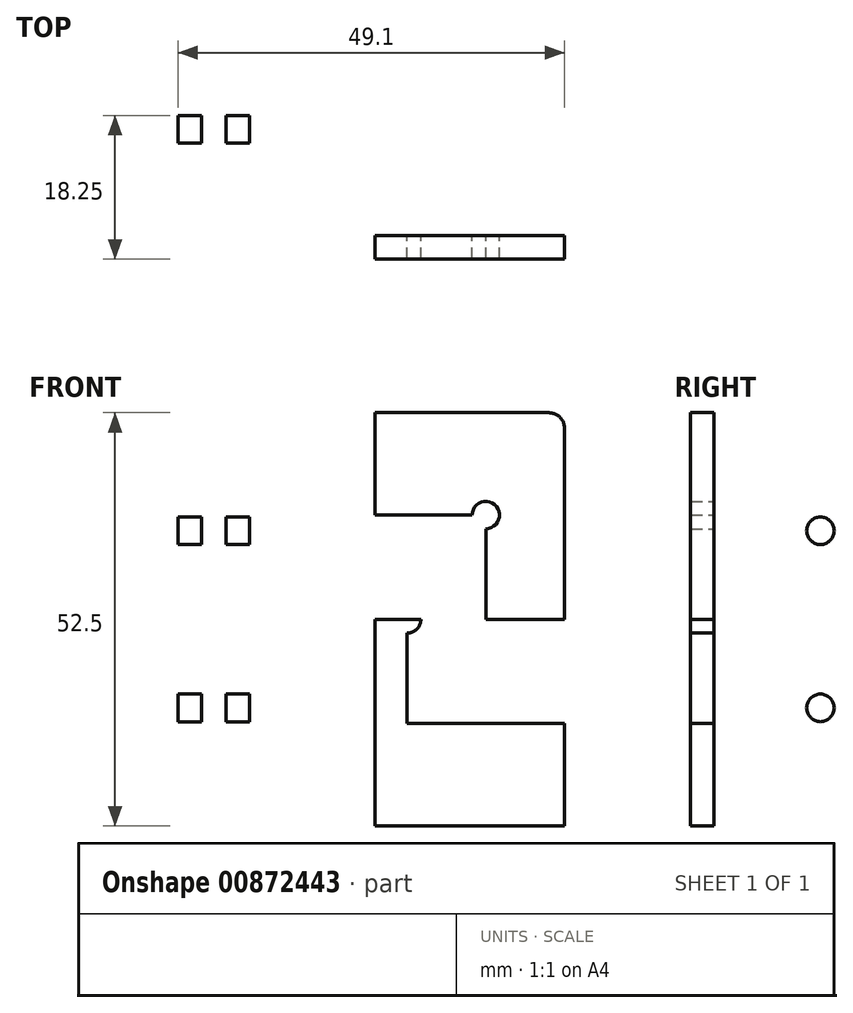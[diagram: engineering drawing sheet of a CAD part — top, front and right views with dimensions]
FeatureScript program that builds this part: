
annotation { "Feature Type Name" : "Feature", "Feature Type Description" : "" }
export const myFeature = defineFeature(function(context is Context, id is Id, definition is map)
    precondition{}
    {
        {
            var Q0;
            Q0=qCreatedBy(makeId("Top.planeOp"),FACE);
            var sketch = newSketch(context, id + "F0", { "sketchPlane" : qUnion([Q0])});
            skLineSegment(sketch, "E0", {"start": v(0, 0) * mm, "end": v(0, 30) * mm});
            skLineSegment(sketch, "E1", {"start": v(0, 30) * mm, "end": v(-3, 30) * mm});
            skLineSegment(sketch, "E2", {"start": v(-3, 30) * mm, "end": v(-3, 0) * mm});
            skLineSegment(sketch, "E3", {"start": v(-3, 0) * mm, "end": v(-6.1, 0) * mm});
            skLineSegment(sketch, "E4", {"start": v(-6.1, 0) * mm, "end": v(-6.1, 30) * mm});
            skLineSegment(sketch, "E5", {"start": v(-6.1, 30) * mm, "end": v(-9.1, 30) * mm});
            skLineSegment(sketch, "E6", {"start": v(-9.1, 30) * mm, "end": v(-9.1, -3) * mm});
            skLineSegment(sketch, "E7", {"start": v(0, 0) * mm, "end": v(40, 0) * mm});
            skLineSegment(sketch, "E8", {"start": v(40, 0) * mm, "end": v(40, -3) * mm});
            skLineSegment(sketch, "E9", {"start": v(-9.1, -3) * mm, "end": v(40, -3) * mm});
            skLineSegment(sketch, "E10", {"start": v(0, 0) * mm, "end": v(-9.1, 0) * mm});
            skSolve(sketch);
        }
        {
            var Q0;
            {var subQ0=sQuery(id+"F0.wireOp",EDGE,"E0");Q0=makeQuery(id+"F0.imprint","IMPRINT",FACE,{"disambiguationData":[TD([[makeQuery(id+"F0.imprint","IMPRINT",EDGE,{"derivedFrom":subQ0}),1.0]])]});}
            var Q1;
            {var subQ0=sQuery(id+"F0.wireOp",EDGE,"E4");Q1=makeQuery(id+"F0.imprint","IMPRINT",FACE,{"disambiguationData":[TD([[makeQuery(id+"F0.imprint","IMPRINT",EDGE,{"derivedFrom":subQ0}),1.0]])]});}
            var Q2;
            {var subQ5=sQuery(id+"F0.wireOp",EDGE,"E3");Q2=makeQuery(id+"F0.imprint","IMPRINT",FACE,{"disambiguationData":[TD([[makeQuery(id+"F0.imprint","IMPRINT",EDGE,{"derivedFrom":subQ5}),1.0]])]});}
            var Q3;
            Q3=sQuery(id+"F0.wireOp",EDGE,"E4");
            var Q4;
            Q4=sQuery(id+"F0.wireOp",EDGE,"E9");
            var Q5;
            Q5=sQuery(id+"F0.wireOp",EDGE,"E7");
            var Q6;
            Q6=sQuery(id+"F0.wireOp",EDGE,"E0");
            var Q7;
            Q7=sQuery(id+"F0.wireOp",EDGE,"E2");
            var Q8;
            Q8=sQuery(id+"F0.wireOp",EDGE,"E6");
            var Q9;
            Q9=sQuery(id+"F0.wireOp",EDGE,"E3");
            var Q10;
            Q10=sQuery(id+"F0.wireOp",EDGE,"E5");
            var Q11;
            Q11=sQuery(id+"F0.wireOp",EDGE,"E8");
            var Q12;
            Q12=sQuery(id+"F0.wireOp",EDGE,"E1");
            extrude(context, id + "F1", {"entities" : qUnion([Q0, Q1, Q2]), "surfaceEntities" : qUnion([Q3, Q4, Q5, Q6, Q7, Q8, Q9, Q10, Q11, Q12]), "depth" : 52.5 * mm, "offsetDistance" : 25 * mm});
        }
        {
            var Q0;
            Q0=makeQuery(id+"F1.opExtrude","SWEPT_FACE",FACE,{"disambiguationData":[OSD([sQuery(id+"F0.wireOp",EDGE,"E6")])]});
            var sketch = newSketch(context, id + "F2", { "sketchPlane" : qUnion([Q0])});
            skLineSegment(sketch, "E11", {"start": v(3, 52.5) * mm, "end": v(3, 0) * mm});
            skLineSegment(sketch, "E12", {"start": v(-13.5, 52.5) * mm, "end": v(-13.5, 0) * mm});
            skLineSegment(sketch, "E13", {"start": v(-13.5, 52.5) * mm, "end": v(-13.5, 37.5) * mm});
            skLineSegment(sketch, "E14", {"start": v(-13.5, 26.25) * mm, "end": v(-13.5, 11.34) * mm});
            skLineSegment(sketch, "E15", {"start": v(-13.5, 0) * mm, "end": v(-13.5, 15) * mm});
            skCircle(sketch, "E16", {"center": v(-13.5, 37.5) * mm, "radius": 1.75 * mm});
            skCircle(sketch, "E17", {"center": v(-13.5, 15) * mm, "radius": 1.75 * mm});
            skSolve(sketch);
        }
        {
            var Q0;
            {var subQ0=sQuery(id+"F2.wireOp",EDGE,"E13");var subQ1=sQuery(id+"F2.wireOp",EDGE,"E12");var subQ2=makeQuery(id+"F2.imprint","INTERSECT",VERTEX,{"derivedFrom":[subQ1,subQ0]});Q0=makeQuery(id+"F2.imprint","IMPRINT",FACE,{"disambiguationData":[TD([[makeQuery(id+"F2.imprint","IMPRINT",EDGE,{"disambiguationData":[TD([[subQ2,-1.0]])],"derivedFrom":subQ1}),-1.0]])]});}
            var Q1;
            {var subQ0=sQuery(id+"F2.wireOp",EDGE,"E13");var subQ1=sQuery(id+"F2.wireOp",EDGE,"E12");var subQ2=makeQuery(id+"F2.imprint","INTERSECT",VERTEX,{"derivedFrom":[subQ1,subQ0]});Q1=makeQuery(id+"F2.imprint","IMPRINT",FACE,{"disambiguationData":[TD([[makeQuery(id+"F2.imprint","IMPRINT",EDGE,{"disambiguationData":[TD([[subQ2,-1.0]])],"derivedFrom":subQ1}),1.0]])]});}
            var Q2;
            {var subQ0=sQuery(id+"F2.wireOp",EDGE,"E15");var subQ1=sQuery(id+"F2.wireOp",EDGE,"E14");var subQ2=makeQuery(id+"F2.imprint","INTERSECT",VERTEX,{"derivedFrom":[subQ1,subQ0]});Q2=makeQuery(id+"F2.imprint","IMPRINT",FACE,{"disambiguationData":[TD([[makeQuery(id+"F2.imprint","IMPRINT",EDGE,{"disambiguationData":[TD([[subQ2,1.0]])],"derivedFrom":subQ1}),1.0]])]});}
            var Q3;
            {var subQ0=sQuery(id+"F2.wireOp",EDGE,"E15");var subQ1=sQuery(id+"F2.wireOp",EDGE,"E14");var subQ2=makeQuery(id+"F2.imprint","INTERSECT",VERTEX,{"derivedFrom":[subQ1,subQ0]});Q3=makeQuery(id+"F2.imprint","IMPRINT",FACE,{"disambiguationData":[TD([[makeQuery(id+"F2.imprint","IMPRINT",EDGE,{"disambiguationData":[TD([[subQ2,1.0]])],"derivedFrom":subQ1}),-1.0]])]});}
            var Q4;
            Q4=sQuery(id+"F2.wireOp",EDGE,"E16");
            var Q5;
            Q5=sQuery(id+"F2.wireOp",EDGE,"E17");
            extrude(context, id + "F3", {"entities" : qUnion([Q0, Q1, Q2, Q3]), "operationType" : NewBodyOperationType.REMOVE, "surfaceEntities" : qUnion([Q4, Q5]), "oppositeDirection" : true, "depth" : 25 * mm, "offsetDistance" : 25 * mm});
        }
        {
            var Q0;
            Q0=makeQuery(id+"F1.opExtrude","SWEPT_FACE",FACE,{"disambiguationData":[OSD([sQuery(id+"F0.wireOp",EDGE,"E7")])]});
            var sketch = newSketch(context, id + "F4", { "sketchPlane" : qUnion([Q0])});
            skLineSegment(sketch, "E18", {"start": v(0, 52.5) * mm, "end": v(-40, 52.5) * mm});
            skLineSegment(sketch, "E19", {"start": v(-40, 0) * mm, "end": v(-30, 0) * mm});
            skLineSegment(sketch, "E20", {"start": v(-30, 0) * mm, "end": v(-20, 0) * mm});
            skLineSegment(sketch, "E21", {"start": v(-20, 0) * mm, "end": v(-10, 0) * mm});
            skLineSegment(sketch, "E22", {"start": v(-20, 0) * mm, "end": v(-20, 52.5) * mm});
            skLineSegment(sketch, "E23", {"start": v(-10, 0) * mm, "end": v(-10, 52.5) * mm});
            skLineSegment(sketch, "E24", {"start": v(-30, 0) * mm, "end": v(-30, 52.5) * mm});
            skLineSegment(sketch, "E25", {"start": v(-40, 52.5) * mm, "end": v(-40, 39.5) * mm});
            skLineSegment(sketch, "E26", {"start": v(-40, 0) * mm, "end": v(-40, 13) * mm});
            skLineSegment(sketch, "E27", {"start": v(-40, 13) * mm, "end": v(-40, 26.25) * mm});
            skLineSegment(sketch, "E28", {"start": v(-40, 26.25) * mm, "end": v(0, 26.25) * mm});
            skLineSegment(sketch, "E29", {"start": v(-40, 13) * mm, "end": v(0, 13) * mm});
            skLineSegment(sketch, "E30", {"start": v(-40, 39.5) * mm, "end": v(0, 39.5) * mm});
            skCircle(sketch, "E31", {"center": v(-30, 39.5) * mm, "radius": 1.75 * mm});
            skCircle(sketch, "E32", {"center": v(-10, 39.5) * mm, "radius": 1.75 * mm});
            skCircle(sketch, "E33", {"center": v(-30, 13) * mm, "radius": 1.75 * mm});
            skCircle(sketch, "E34", {"center": v(-10, 13) * mm, "radius": 1.75 * mm});
            skCircle(sketch, "E35", {"center": v(-20, 26.25) * mm, "radius": 1.75 * mm});
            skSolve(sketch);
        }
        {
            var Q0;
            {var subQ0=sQuery(id+"F4.wireOp",EDGE,"E31");var subQ1=sQuery(id+"F4.wireOp",EDGE,"E24");var subQ2=makeQuery(id+"F4.imprint","INTERSECT",VERTEX,{"disambiguationData":[OD(0.0)],"derivedFrom":[subQ1,subQ0]});Q0=makeQuery(id+"F4.imprint","IMPRINT",FACE,{"disambiguationData":[TD([[makeQuery(id+"F4.imprint","IMPRINT",EDGE,{"disambiguationData":[TD([[subQ2,-1.0]])],"derivedFrom":subQ1}),-1.0]])]});}
            var Q1;
            {var subQ0=sQuery(id+"F4.wireOp",EDGE,"E30");var subQ1=sQuery(id+"F4.wireOp",EDGE,"E24");var subQ2=makeQuery(id+"F4.imprint","INTERSECT",VERTEX,{"derivedFrom":[subQ1,subQ0]});Q1=makeQuery(id+"F4.imprint","IMPRINT",FACE,{"disambiguationData":[TD([[makeQuery(id+"F4.imprint","IMPRINT",EDGE,{"disambiguationData":[TD([[subQ2,-1.0]])],"derivedFrom":subQ1}),-1.0]])]});}
            var Q2;
            {var subQ0=sQuery(id+"F4.wireOp",EDGE,"E30");var subQ1=sQuery(id+"F4.wireOp",EDGE,"E24");var subQ2=makeQuery(id+"F4.imprint","INTERSECT",VERTEX,{"derivedFrom":[subQ1,subQ0]});Q2=makeQuery(id+"F4.imprint","IMPRINT",FACE,{"disambiguationData":[TD([[makeQuery(id+"F4.imprint","IMPRINT",EDGE,{"disambiguationData":[TD([[subQ2,-1.0]])],"derivedFrom":subQ1}),1.0]])]});}
            var Q3;
            {var subQ0=sQuery(id+"F4.wireOp",EDGE,"E31");var subQ1=sQuery(id+"F4.wireOp",EDGE,"E24");var subQ2=makeQuery(id+"F4.imprint","INTERSECT",VERTEX,{"disambiguationData":[OD(0.0)],"derivedFrom":[subQ1,subQ0]});Q3=makeQuery(id+"F4.imprint","IMPRINT",FACE,{"disambiguationData":[TD([[makeQuery(id+"F4.imprint","IMPRINT",EDGE,{"disambiguationData":[TD([[subQ2,-1.0]])],"derivedFrom":subQ1}),1.0]])]});}
            var Q4;
            {var subQ0=sQuery(id+"F4.wireOp",EDGE,"E32");var subQ1=sQuery(id+"F4.wireOp",EDGE,"E23");var subQ2=makeQuery(id+"F4.imprint","INTERSECT",VERTEX,{"disambiguationData":[OD(0.0)],"derivedFrom":[subQ1,subQ0]});Q4=makeQuery(id+"F4.imprint","IMPRINT",FACE,{"disambiguationData":[TD([[makeQuery(id+"F4.imprint","IMPRINT",EDGE,{"disambiguationData":[TD([[subQ2,-1.0]])],"derivedFrom":subQ1}),1.0]])]});}
            var Q5;
            {var subQ0=sQuery(id+"F4.wireOp",EDGE,"E32");var subQ1=sQuery(id+"F4.wireOp",EDGE,"E23");var subQ2=makeQuery(id+"F4.imprint","INTERSECT",VERTEX,{"disambiguationData":[OD(0.0)],"derivedFrom":[subQ1,subQ0]});Q5=makeQuery(id+"F4.imprint","IMPRINT",FACE,{"disambiguationData":[TD([[makeQuery(id+"F4.imprint","IMPRINT",EDGE,{"disambiguationData":[TD([[subQ2,-1.0]])],"derivedFrom":subQ1}),-1.0]])]});}
            var Q6;
            {var subQ0=sQuery(id+"F4.wireOp",EDGE,"E30");var subQ1=sQuery(id+"F4.wireOp",EDGE,"E23");var subQ2=makeQuery(id+"F4.imprint","INTERSECT",VERTEX,{"derivedFrom":[subQ1,subQ0]});Q6=makeQuery(id+"F4.imprint","IMPRINT",FACE,{"disambiguationData":[TD([[makeQuery(id+"F4.imprint","IMPRINT",EDGE,{"disambiguationData":[TD([[subQ2,-1.0]])],"derivedFrom":subQ1}),-1.0]])]});}
            var Q7;
            {var subQ0=sQuery(id+"F4.wireOp",EDGE,"E30");var subQ1=sQuery(id+"F4.wireOp",EDGE,"E23");var subQ2=makeQuery(id+"F4.imprint","INTERSECT",VERTEX,{"derivedFrom":[subQ1,subQ0]});Q7=makeQuery(id+"F4.imprint","IMPRINT",FACE,{"disambiguationData":[TD([[makeQuery(id+"F4.imprint","IMPRINT",EDGE,{"disambiguationData":[TD([[subQ2,-1.0]])],"derivedFrom":subQ1}),1.0]])]});}
            var Q8;
            {var subQ0=sQuery(id+"F4.wireOp",EDGE,"E29");var subQ1=sQuery(id+"F4.wireOp",EDGE,"E23");var subQ2=makeQuery(id+"F4.imprint","INTERSECT",VERTEX,{"derivedFrom":[subQ1,subQ0]});Q8=makeQuery(id+"F4.imprint","IMPRINT",FACE,{"disambiguationData":[TD([[makeQuery(id+"F4.imprint","IMPRINT",EDGE,{"disambiguationData":[TD([[subQ2,-1.0]])],"derivedFrom":subQ1}),1.0]])]});}
            var Q9;
            {var subQ0=sQuery(id+"F4.wireOp",EDGE,"E29");var subQ1=sQuery(id+"F4.wireOp",EDGE,"E23");var subQ2=makeQuery(id+"F4.imprint","INTERSECT",VERTEX,{"derivedFrom":[subQ1,subQ0]});Q9=makeQuery(id+"F4.imprint","IMPRINT",FACE,{"disambiguationData":[TD([[makeQuery(id+"F4.imprint","IMPRINT",EDGE,{"disambiguationData":[TD([[subQ2,-1.0]])],"derivedFrom":subQ1}),-1.0]])]});}
            var Q10;
            {var subQ0=sQuery(id+"F4.wireOp",EDGE,"E34");var subQ1=sQuery(id+"F4.wireOp",EDGE,"E23");var subQ2=makeQuery(id+"F4.imprint","INTERSECT",VERTEX,{"disambiguationData":[OD(0.0)],"derivedFrom":[subQ1,subQ0]});Q10=makeQuery(id+"F4.imprint","IMPRINT",FACE,{"disambiguationData":[TD([[makeQuery(id+"F4.imprint","IMPRINT",EDGE,{"disambiguationData":[TD([[subQ2,-1.0]])],"derivedFrom":subQ1}),-1.0]])]});}
            var Q11;
            {var subQ0=sQuery(id+"F4.wireOp",EDGE,"E34");var subQ1=sQuery(id+"F4.wireOp",EDGE,"E23");var subQ2=makeQuery(id+"F4.imprint","INTERSECT",VERTEX,{"disambiguationData":[OD(0.0)],"derivedFrom":[subQ1,subQ0]});Q11=makeQuery(id+"F4.imprint","IMPRINT",FACE,{"disambiguationData":[TD([[makeQuery(id+"F4.imprint","IMPRINT",EDGE,{"disambiguationData":[TD([[subQ2,-1.0]])],"derivedFrom":subQ1}),1.0]])]});}
            var Q12;
            {var subQ0=sQuery(id+"F4.wireOp",EDGE,"E33");var subQ1=sQuery(id+"F4.wireOp",EDGE,"E24");var subQ2=makeQuery(id+"F4.imprint","INTERSECT",VERTEX,{"disambiguationData":[OD(0.0)],"derivedFrom":[subQ1,subQ0]});Q12=makeQuery(id+"F4.imprint","IMPRINT",FACE,{"disambiguationData":[TD([[makeQuery(id+"F4.imprint","IMPRINT",EDGE,{"disambiguationData":[TD([[subQ2,-1.0]])],"derivedFrom":subQ1}),-1.0]])]});}
            var Q13;
            {var subQ0=sQuery(id+"F4.wireOp",EDGE,"E33");var subQ1=sQuery(id+"F4.wireOp",EDGE,"E24");var subQ2=makeQuery(id+"F4.imprint","INTERSECT",VERTEX,{"disambiguationData":[OD(0.0)],"derivedFrom":[subQ1,subQ0]});Q13=makeQuery(id+"F4.imprint","IMPRINT",FACE,{"disambiguationData":[TD([[makeQuery(id+"F4.imprint","IMPRINT",EDGE,{"disambiguationData":[TD([[subQ2,-1.0]])],"derivedFrom":subQ1}),1.0]])]});}
            var Q14;
            {var subQ0=sQuery(id+"F4.wireOp",EDGE,"E29");var subQ1=sQuery(id+"F4.wireOp",EDGE,"E24");var subQ2=makeQuery(id+"F4.imprint","INTERSECT",VERTEX,{"derivedFrom":[subQ1,subQ0]});Q14=makeQuery(id+"F4.imprint","IMPRINT",FACE,{"disambiguationData":[TD([[makeQuery(id+"F4.imprint","IMPRINT",EDGE,{"disambiguationData":[TD([[subQ2,-1.0]])],"derivedFrom":subQ1}),1.0]])]});}
            var Q15;
            {var subQ0=sQuery(id+"F4.wireOp",EDGE,"E29");var subQ1=sQuery(id+"F4.wireOp",EDGE,"E24");var subQ2=makeQuery(id+"F4.imprint","INTERSECT",VERTEX,{"derivedFrom":[subQ1,subQ0]});Q15=makeQuery(id+"F4.imprint","IMPRINT",FACE,{"disambiguationData":[TD([[makeQuery(id+"F4.imprint","IMPRINT",EDGE,{"disambiguationData":[TD([[subQ2,-1.0]])],"derivedFrom":subQ1}),-1.0]])]});}
            var Q16;
            {var subQ0=sQuery(id+"F4.wireOp",EDGE,"E35");var subQ1=sQuery(id+"F4.wireOp",EDGE,"E22");var subQ2=makeQuery(id+"F4.imprint","INTERSECT",VERTEX,{"disambiguationData":[OD(0.0)],"derivedFrom":[subQ1,subQ0]});Q16=makeQuery(id+"F4.imprint","IMPRINT",FACE,{"disambiguationData":[TD([[makeQuery(id+"F4.imprint","IMPRINT",EDGE,{"disambiguationData":[TD([[subQ2,-1.0]])],"derivedFrom":subQ1}),1.0]])]});}
            var Q17;
            {var subQ0=sQuery(id+"F4.wireOp",EDGE,"E35");var subQ1=sQuery(id+"F4.wireOp",EDGE,"E22");var subQ2=makeQuery(id+"F4.imprint","INTERSECT",VERTEX,{"disambiguationData":[OD(0.0)],"derivedFrom":[subQ1,subQ0]});Q17=makeQuery(id+"F4.imprint","IMPRINT",FACE,{"disambiguationData":[TD([[makeQuery(id+"F4.imprint","IMPRINT",EDGE,{"disambiguationData":[TD([[subQ2,-1.0]])],"derivedFrom":subQ1}),-1.0]])]});}
            var Q18;
            {var subQ0=sQuery(id+"F4.wireOp",EDGE,"E28");var subQ1=sQuery(id+"F4.wireOp",EDGE,"E22");var subQ2=makeQuery(id+"F4.imprint","INTERSECT",VERTEX,{"derivedFrom":[subQ1,subQ0]});Q18=makeQuery(id+"F4.imprint","IMPRINT",FACE,{"disambiguationData":[TD([[makeQuery(id+"F4.imprint","IMPRINT",EDGE,{"disambiguationData":[TD([[subQ2,-1.0]])],"derivedFrom":subQ1}),-1.0]])]});}
            var Q19;
            {var subQ0=sQuery(id+"F4.wireOp",EDGE,"E28");var subQ1=sQuery(id+"F4.wireOp",EDGE,"E22");var subQ2=makeQuery(id+"F4.imprint","INTERSECT",VERTEX,{"derivedFrom":[subQ1,subQ0]});Q19=makeQuery(id+"F4.imprint","IMPRINT",FACE,{"disambiguationData":[TD([[makeQuery(id+"F4.imprint","IMPRINT",EDGE,{"disambiguationData":[TD([[subQ2,-1.0]])],"derivedFrom":subQ1}),1.0]])]});}
            extrude(context, id + "F5", {"entities" : qUnion([Q0, Q1, Q2, Q3, Q4, Q5, Q6, Q7, Q8, Q9, Q10, Q11, Q12, Q13, Q14, Q15, Q16, Q17, Q18, Q19]), "operationType" : NewBodyOperationType.REMOVE, "oppositeDirection" : true, "depth" : 25 * mm, "offsetDistance" : 25 * mm});
        }
        {
            var Q0;
            Q0=makeQuery(id+"F1.opExtrude","CAP_EDGE",EDGE,{"disambiguationData":[OSD([sQuery(id+"F0.wireOp",EDGE,"E8")])],"isStart":false});
            var Q1;
            Q1=makeQuery(id+"F1.opExtrude","SWEPT_EDGE",EDGE,{"disambiguationData":[OSD([sQuery(id+"F0.wireOp",EDGE,"E5"),sQuery(id+"F0.wireOp",EDGE,"E6")])]});
            var Q2;
            Q2=makeQuery(id+"F1.opExtrude","CAP_EDGE",EDGE,{"disambiguationData":[OSD([sQuery(id+"F0.wireOp",EDGE,"E6")])],"isStart":false});
            var Q3;
            Q3=makeQuery(id+"F1.opExtrude","CAP_EDGE",EDGE,{"disambiguationData":[OSD([sQuery(id+"F0.wireOp",EDGE,"E5")])],"isStart":false});
            fillet(context, id + "F6", {"entities" : qUnion([Q0, Q1, Q2, Q3]), "radius" : 2 * mm, "tangentPropagation" : true, "allowEdgeOverflow" : false});
        }
    });
